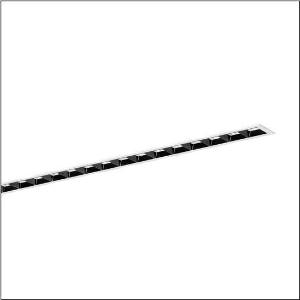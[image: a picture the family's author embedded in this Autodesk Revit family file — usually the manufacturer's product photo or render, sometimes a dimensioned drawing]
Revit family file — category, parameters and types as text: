
# Revit family: silica_r__21_51mx12da44wb_905f
name_source: partatom
category: Lighting Fixtures
units: mm (PartAtom-declared; Revit-internal decimal feet)

## family parameters
Cut with Voids When Loaded = No
Host = Face
Light Source = No
Part Type = Normal
Room Calculation Point = No
Round Connector Dimension = Use Diameter
Shared = No

## types (1)
- --- (1 x LED, 4320 lm, 25.6 W, 4000K)
    Apparent Load = 26 VA
    CIE Flux Codes = 86 100 100 100 100
    Color Rendering = 80
    Color Temperature = 4000K
    Default Elevation = 1800 mm
    Description = Silica® 21, office luminaire, primary light control with darklight reflector, of PMMA, black, CAT 2 (L<= 3000cd/m²), light emission: direct distribution, primary light characteristic: symmetric, installation type: recessed, LED, rated luminous flux: 4.320lm, luminous efficacy: 169lm/W, light colour: 840, colour temperature: 4000K, with terminal, 3+2-pole, max. 2.5mm², mains connection: 220..240V, AC, 50/60Hz, rated input power: 25.6W, luminaire housing, of aluminium, traffic white (RAL 9016), length: 1.228mm, width: 79mm, height: 53mm, protection rating (complete): IP20, insulation class (complete): insulation class I (protective earthing), certification: CE, permissible operating ambient temperature: 0..+35°C, standard: EN 50419, packaging unit: 1 piece
    Height = 0 mm  [stored 0 ft]
    Lamp = 1 x LED
    Lamp Light Flux = 4320 lm
    Lamp Power = 25.6 W
    Lamp count = 1
    Length = 1227 mm
    Luminous efficacy = 169 lm/W
    Manufacturer = Siteco
    ModVariant = No
    Model = 51MX12DA44WB
    Mounting Place = Ceiling
    Mounting Type = Recessed
    Number of Poles = 1
    OnlyDefault = Yes
    Power Factor = 1
    Product Name = Silica® 21
    Product group = office luminaire | ceiling recessed
    ProductGroupID = 401
    Protection Class = Protection class I
    Protection Degree = IP 20
    RLX_Detail_Level = 1
    RLX_Emergency_Light_Flux = 0 lm
    RLX_Emergency_Type = 0
    RLX_Emergency_Type_DB = No
    RlxData = <blob elided: 39825 chars, md5=70fcd6a0>
    Socket = socket
    Standby Power = 0 W
    System Light Flux = 4320 lm
    System Power = 26 W
    Type Comments = factory setting: luminous flux: 100 % | dim-lin: 254 | 367 mA
    Type Image = l_1313610.jpg
    URL = http://relux.com
    VarID = @adj_073903
    Voltage = 0 V
    Weight = 0.00 kg
    Width = 79 mm

note: [stored X ft] marks values corroborated as IEEE doubles in the binary element streams (Revit-internal decimal feet)

## geometry (parser evidence)
native form markers: Blend x4, Sweep x10
no freeform markers — native parametric forms only
